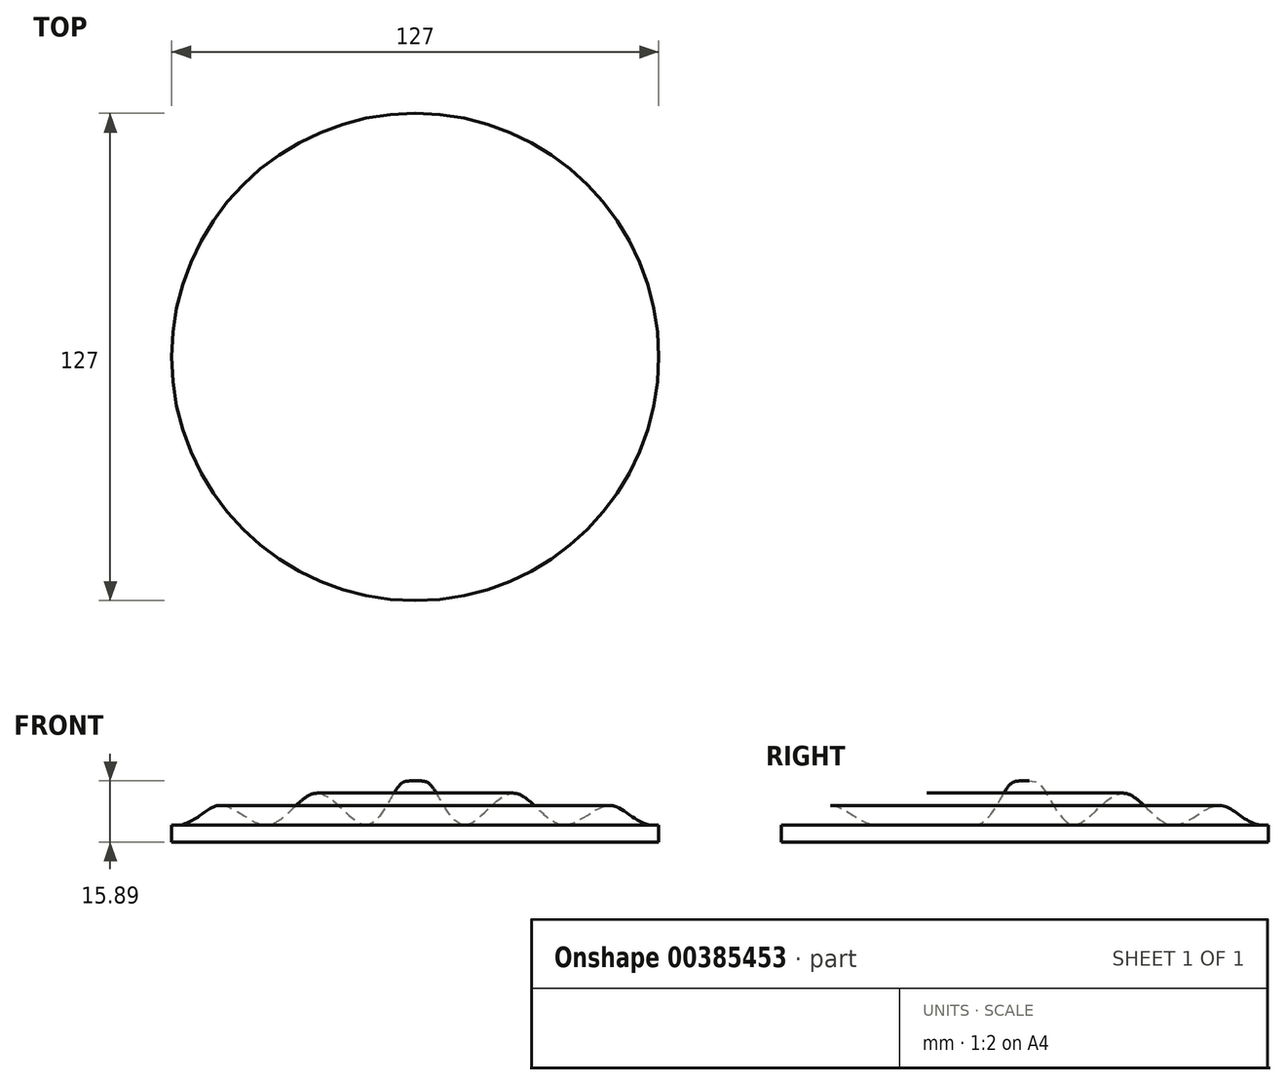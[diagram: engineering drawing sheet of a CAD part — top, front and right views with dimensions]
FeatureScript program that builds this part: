
annotation { "Feature Type Name" : "Feature", "Feature Type Description" : "" }
export const myFeature = defineFeature(function(context is Context, id is Id, definition is map)
    precondition{}
    {
        {
            var Q0;
            Q0=qCreatedBy(makeId("Right.planeOp"),FACE);
            var sketch = newSketch(context, id + "F0", { "sketchPlane" : qUnion([Q0])});
            skLineSegment(sketch, "E0", {"start": v(0, 0) * mm, "end": v(0, 19.05) * mm});
            skLineSegment(sketch, "E1", {"start": v(0, 19.05) * mm, "end": v(63.5, 19.05) * mm});
            skLineSegment(sketch, "E2", {"start": v(63.5, 19.05) * mm, "end": v(63.5, 0) * mm});
            skLineSegment(sketch, "E3", {"start": v(63.5, 0) * mm, "end": v(0, 0) * mm});
            skFitSpline(sketch, "E4", {"points": [v(0, 15.88) * mm, v(4.2, 14.65) * mm, v(12.7, 4.44) * mm, v(25.4, 12.7) * mm, v(38.1, 4.44) * mm, v(50.8, 9.53) * mm, v(63.5, 4.44) * mm], "startDerivative": vector(55.5, 0) * mm, "endDerivative": vector(93.52, 16.05) * mm});
            skLineSegment(sketch, "E5", {"start": v(63.5, 4.44) * mm, "end": v(0, 4.44) * mm, "construction": true});
            skSolve(sketch);
        }
        {
            var Q0;
            {var subQ0=sQuery(id+"F0.wireOp",EDGE,"E3");Q0=makeQuery(id+"F0.imprint","IMPRINT",FACE,{"disambiguationData":[TD([[makeQuery(id+"F0.imprint","IMPRINT",EDGE,{"derivedFrom":subQ0}),-1.0]])]});}
            var Q1;
            Q1=sQuery(id+"F0.wireOp",EDGE,"E0");
            revolve(context, id + "F1", {"entities" : qUnion([Q0]), "axis" : qUnion([Q1]), "revolveType" : RevolveType.FULL});
        }
    });
